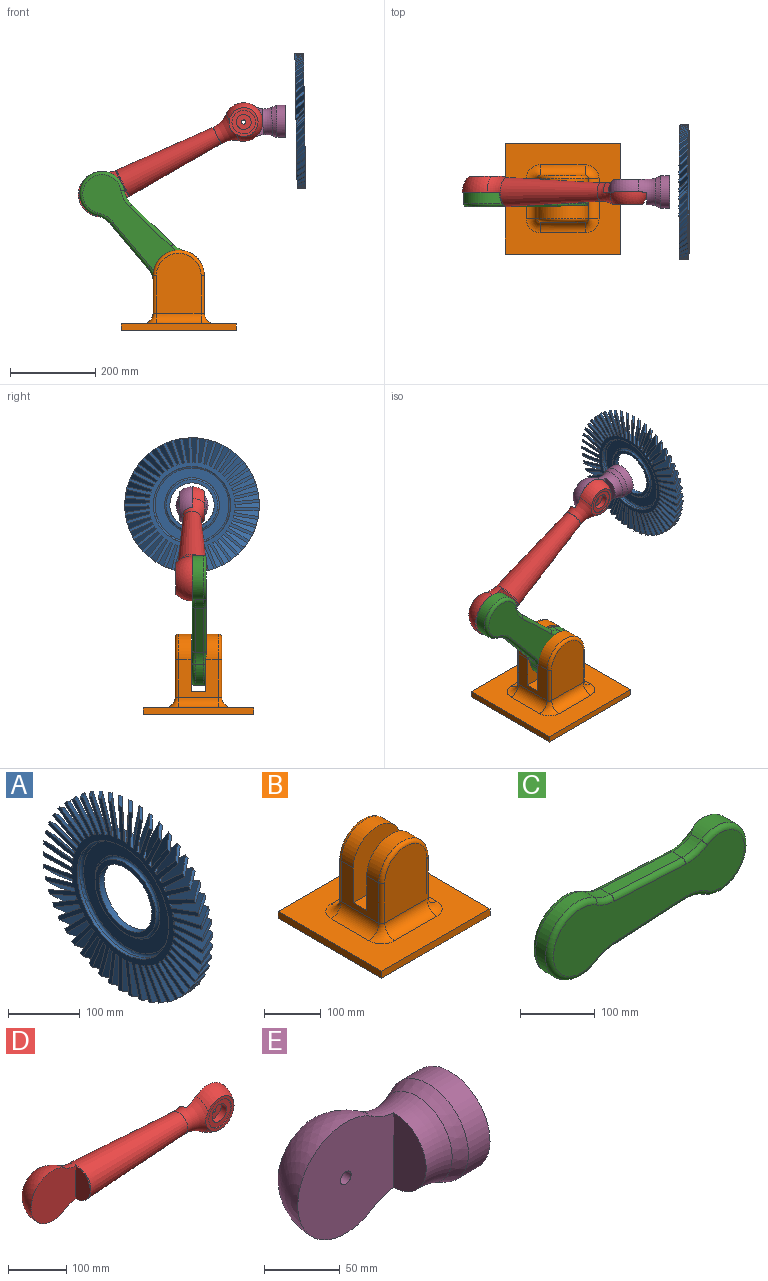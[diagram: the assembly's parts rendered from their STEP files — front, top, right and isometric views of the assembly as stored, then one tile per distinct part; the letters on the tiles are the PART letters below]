
ASSEMBLY  parts=5 mates=4
PART A: 209 faces, bbox 20x315.1x315 mm
  f0: cylinder r=90.5mm len=181mm, axis (-1,0,0), area 2843.1mm2, adj f1,f2
  f1: plane 314.99x314.87mm, normal (1,0,0), area 25655mm2, adj f0,f3,f4,f5,f6,f7,f8,f9
  f2: torus R=86.5mm, axis (-1,0,0), area 3515.4mm2, adj f0,f199
  f3: cylinder r=157.5mm len=25.8mm, axis (-1,0,0), area 130.3mm2, adj f1,f4,f198,f200
  f4: plane 60.82x29.89mm, normal (-0.71,0.7,-0.13), area 1610.9mm2, adj f1,f3,f5,f200
  f5: plane 24.82x20mm, normal (0,0.25,0.97), area 113.1mm2, adj f1,f4,f6,f200
  f6: plane 59.18x37.22mm, normal (0.71,-0.67,0.23), area 1598.6mm2, adj f1,f5,f7,f200
  f7: cylinder r=157.5mm len=24.84mm, axis (-1,0,0), area 130.3mm2, adj f1,f6,f8,f200
  f8: plane 61.46x36.15mm, normal (-0.71,0.67,-0.22), area 1610.9mm2, adj f1,f7,f9,f200
  f9: plane 23.78x20mm, normal (0,0.38,0.93), area 113.1mm2, adj f1,f8,f10,f200
  f10: plane 58.82x43mm, normal (0.71,-0.64,0.31), area 1598.6mm2, adj f1,f9,f11,f200
  f11: cylinder r=157.5mm len=23.47mm, axis (-1,0,0), area 130.3mm2, adj f1,f10,f12,f200
  f12: plane 61.08x41.82mm, normal (-0.71,0.64,-0.3), area 1610.9mm2, adj f1,f11,f13,f200
  f13: plane 22.36x20mm, normal (0,0.49,0.87), area 113.1mm2, adj f1,f12,f14,f200
  f14: plane 57.5x48.08mm, normal (0.71,-0.59,0.39), area 1598.6mm2, adj f1,f13,f15,f200
  f15: cylinder r=157.5mm len=21.71mm, axis (-1,0,0), area 130.3mm2, adj f1,f14,f16,f200
  f16: plane 59.71x46.8mm, normal (-0.71,0.6,-0.38), area 1610.9mm2, adj f1,f15,f17,f200
  f17: plane 20.56x20mm, normal (0,0.6,0.8), area 113.1mm2, adj f1,f16,f18,f200
  f18: plane 55.23x52.37mm, normal (0.71,-0.54,0.46), area 1598.6mm2, adj f1,f17,f19,f200
  f19: cylinder r=157.5mm len=20mm, axis (-1,0,0), area 130.3mm2, adj f1,f18,f20,f200
  f20: plane 57.35x51.02mm, normal (-0.71,0.54,-0.46), area 1610.9mm2, adj f1,f19,f21,f200
  f21: plane 20x18.43mm, normal (0,0.7,0.72), area 113.1mm2, adj f1,f20,f22,f200
  f22: plane 55.79x52.05mm, normal (0.71,-0.47,0.53), area 1598.6mm2, adj f1,f21,f23,f200
  f23: cylinder r=157.5mm len=20.15mm, axis (-1,0,0), area 130.3mm2, adj f1,f22,f24,f200
  f24: plane 54.39x54.05mm, normal (-0.71,0.48,-0.52), area 1610.9mm2, adj f1,f23,f25,f200
  f25: plane 20.06x20mm, normal (0,0.78,0.62), area 113.1mm2, adj f1,f24,f26,f200
  f26: plane 58.31x48.02mm, normal (0.71,-0.4,0.58), area 1598.6mm2, adj f1,f25,f27,f200
  f27: cylinder r=157.5mm len=22.18mm, axis (-1,0,0), area 130.3mm2, adj f1,f26,f28,f200
  f28: plane 56.88x49.87mm, normal (-0.71,0.41,-0.58), area 1610.9mm2, adj f1,f27,f29,f200
  f29: plane 21.94x20mm, normal (0,0.86,0.52), area 113.1mm2, adj f1,f28,f30,f200
  f30: plane 59.86x43.2mm, normal (0.71,-0.32,0.63), area 1598.6mm2, adj f1,f29,f31,f200
  f31: cylinder r=157.5mm len=23.84mm, axis (-1,0,0), area 130.3mm2, adj f1,f30,f32,f200
  f32: plane 58.43x44.86mm, normal (-0.71,0.33,-0.63), area 1610.9mm2, adj f1,f31,f33,f200
  f33: plane 23.46x20mm, normal (0,0.91,0.4), area 113.1mm2, adj f1,f32,f34,f200
  f34: plane 60.43x37.68mm, normal (0.71,-0.24,0.67), area 1598.6mm2, adj f1,f33,f35,f200
  f35: cylinder r=157.5mm len=25.12mm, axis (-1,0,0), area 130.3mm2, adj f1,f34,f36,f200
  f36: plane 59.02x39.13mm, normal (-0.71,0.25,-0.66), area 1610.9mm2, adj f1,f35,f37,f200
  f37: plane 24.6x20mm, normal (0,0.96,0.28), area 113.1mm2, adj f1,f36,f38,f200
  f38: plane 60.01x31.53mm, normal (0.71,-0.15,0.69), area 1598.6mm2, adj f1,f37,f39,f200
  f39: cylinder r=157.5mm len=25.98mm, axis (-1,0,0), area 130.3mm2, adj f1,f38,f40,f200
  f40: plane 58.64x32.74mm, normal (-0.71,0.16,-0.69), area 1610.9mm2, adj f1,f39,f41,f200
  f41: plane 25.33x20mm, normal (0,0.99,0.16), area 113.1mm2, adj f1,f40,f42,f200
  f42: plane 58.6x24.87mm, normal (0.71,-0.06,0.71), area 1598.6mm2, adj f1,f41,f43,f200
  f43: cylinder r=157.5mm len=26.41mm, axis (-1,0,0), area 130.3mm2, adj f1,f42,f44,f200
  f44: plane 57.35x25.83mm, normal (-0.71,0.07,-0.7), area 1610.9mm2, adj f1,f43,f45,f200
  f45: plane 25.64x20mm, normal (0,1,0.03), area 113.1mm2, adj f1,f44,f46,f200
  f46: plane 57.14x22.14mm, normal (0.71,0.03,0.71), area 1598.6mm2, adj f1,f45,f47,f200
  f47: cylinder r=157.5mm len=26.41mm, axis (-1,0,0), area 130.3mm2, adj f1,f46,f48,f200
  f48: plane 58.63x21.39mm, normal (-0.71,-0.02,-0.71), area 1610.9mm2, adj f1,f47,f49,f200
  f49: plane 25.54x20mm, normal (0,1,-0.1), area 113.1mm2, adj f1,f48,f50,f200
  f50: plane 58.26x29.15mm, normal (0.71,0.12,0.7), area 1598.6mm2, adj f1,f49,f51,f200
  f51: cylinder r=157.5mm len=25.98mm, axis (-1,0,0), area 130.3mm2, adj f1,f50,f52,f200
  f52: plane 60.5x28.25mm, normal (-0.71,-0.11,-0.7), area 1610.9mm2, adj f1,f51,f53,f200
  f53: plane 25.01x20mm, normal (0,0.97,-0.22), area 113.1mm2, adj f1,f52,f54,f200
  f54: plane 59.12x35.68mm, normal (0.71,0.21,0.68), area 1598.6mm2, adj f1,f53,f55,f200
  f55: cylinder r=157.5mm len=25.12mm, axis (-1,0,0), area 130.3mm2, adj f1,f54,f56,f200
  f56: plane 61.39x34.64mm, normal (-0.71,-0.2,-0.68), area 1610.9mm2, adj f1,f55,f57,f200
  f57: plane 24.08x20mm, normal (0,0.94,-0.35), area 113.1mm2, adj f1,f56,f58,f200
  f58: plane 59x41.62mm, normal (0.71,0.29,0.65), area 1598.6mm2, adj f1,f57,f59,f200
  f59: cylinder r=157.5mm len=23.85mm, axis (-1,0,0), area 130.3mm2, adj f1,f58,f60,f200
  f60: plane 61.27x40.47mm, normal (-0.71,-0.28,-0.65), area 1610.9mm2, adj f1,f59,f61,f200
  f61: plane 22.75x20mm, normal (0,0.89,-0.46), area 113.1mm2, adj f1,f60,f62,f200
  f62: plane 57.92x46.88mm, normal (0.71,0.37,0.6), area 1598.6mm2, adj f1,f61,f63,f200
  f63: cylinder r=157.5mm len=22.18mm, axis (-1,0,0), area 130.3mm2, adj f1,f62,f64,f200
  f64: plane 60.14x45.63mm, normal (-0.71,-0.36,-0.61), area 1610.9mm2, adj f1,f63,f65,f200
  f65: plane 21.04x20mm, normal (0,0.82,-0.57), area 113.1mm2, adj f1,f64,f66,f200
  f66: plane 55.88x51.37mm, normal (0.71,0.45,0.55), area 1598.6mm2, adj f1,f65,f67,f200
  f67: cylinder r=157.5mm len=20.16mm, axis (-1,0,0), area 130.3mm2, adj f1,f66,f68,f200
  f68: plane 58.03x50.04mm, normal (-0.71,-0.44,-0.56), area 1610.9mm2, adj f1,f67,f69,f200
  f69: plane 20x18.99mm, normal (0,0.74,-0.67), area 113.1mm2, adj f1,f68,f70,f200
  f70: plane 55.02x52.93mm, normal (0.71,0.51,0.49), area 1598.6mm2, adj f1,f69,f71,f200
  f71: cylinder r=157.5mm len=20mm, axis (-1,0,0), area 130.3mm2, adj f1,f70,f72,f200
  f72: plane 54.96x53.63mm, normal (-0.71,-0.51,-0.5), area 1610.9mm2, adj f1,f71,f73,f200
  f73: plane 20x19.54mm, normal (0,0.65,-0.76), area 113.1mm2, adj f1,f72,f74,f200
  f74: plane 57.77x49.11mm, normal (0.71,0.57,0.42), area 1598.6mm2, adj f1,f73,f75,f200
  f75: cylinder r=157.5mm len=21.7mm, axis (-1,0,0), area 130.3mm2, adj f1,f74,f76,f200
  f76: plane 56.34x50.99mm, normal (-0.71,-0.56,-0.43), area 1610.9mm2, adj f1,f75,f77,f200
  f77: plane 21.5x20mm, normal (0,0.55,-0.84), area 113.1mm2, adj f1,f76,f78,f200
  f78: plane 59.56x44.48mm, normal (0.71,0.62,0.34), area 1598.6mm2, adj f1,f77,f79,f200
  f79: cylinder r=157.5mm len=23.46mm, axis (-1,0,0), area 130.3mm2, adj f1,f78,f80,f200
  f80: plane 58.13x46.19mm, normal (-0.71,-0.61,-0.35), area 1610.9mm2, adj f1,f79,f81,f200
  f81: plane 23.12x20mm, normal (0,0.43,-0.9), area 113.1mm2, adj f1,f80,f82,f200
  f82: plane 60.38x39.12mm, normal (0.71,0.66,0.26), area 1598.6mm2, adj f1,f81,f83,f200
  f83: cylinder r=157.5mm len=24.84mm, axis (-1,0,0), area 130.3mm2, adj f1,f82,f84,f200
  f84: plane 58.96x40.62mm, normal (-0.71,-0.65,-0.27), area 1610.9mm2, adj f1,f83,f85,f200
  f85: plane 24.35x20mm, normal (0,0.32,-0.95), area 113.1mm2, adj f1,f84,f86,f200
  f86: plane 60.21x33.12mm, normal (0.71,0.69,0.18), area 1598.6mm2, adj f1,f85,f87,f200
  f87: cylinder r=157.5mm len=25.8mm, axis (-1,0,0), area 130.3mm2, adj f1,f86,f88,f200
  f88: plane 58.82x34.39mm, normal (-0.71,-0.68,-0.18), area 1610.9mm2, adj f1,f87,f89,f200
  f89: plane 25.18x20mm, normal (0,0.19,-0.98), area 113.1mm2, adj f1,f88,f90,f200
  f90: plane 59.05x26.57mm, normal (0.71,0.7,0.09), area 1598.6mm2, adj f1,f89,f91,f200
  f91: cylinder r=157.5mm len=26.34mm, axis (-1,0,0), area 130.3mm2, adj f1,f90,f92,f200
  f92: plane 57.72x27.6mm, normal (-0.71,-0.7,-0.1), area 1610.9mm2, adj f1,f91,f93,f200
  f93: plane 25.6x20mm, normal (0,0.06,-1), area 113.1mm2, adj f1,f92,f94,f200
  f94: plane 57.37x20.32mm, normal (0.71,0.71,0), area 1598.6mm2, adj f1,f93,f95,f200
  f95: cylinder r=157.5mm len=26.45mm, axis (-1,0,0), area 130.3mm2, adj f1,f94,f96,f200
  f96: plane 58.03x20.35mm, normal (-0.71,-0.71,0), area 1610.9mm2, adj f1,f95,f97,f200
  f97: plane 25.6x20mm, normal (0,-0.06,-1), area 113.1mm2, adj f1,f96,f98,f200
  f98: plane 57.9x27.43mm, normal (0.71,0.7,-0.1), area 1598.6mm2, adj f1,f97,f99,f200
  f99: cylinder r=157.5mm len=26.13mm, axis (-1,0,0), area 130.3mm2, adj f1,f98,f100,f200
  f100: plane 60.13x26.57mm, normal (-0.71,-0.7,0.09), area 1610.9mm2, adj f1,f99,f101,f200
  f101: plane 25.18x20mm, normal (0,-0.19,-0.98), area 113.1mm2, adj f1,f100,f102,f200
  f102: plane 59x34.1mm, normal (0.71,0.68,-0.18), area 1598.6mm2, adj f1,f101,f103,f200
  f103: cylinder r=157.5mm len=25.37mm, axis (-1,0,0), area 130.3mm2, adj f1,f102,f104,f200
  f104: plane 61.26x33.09mm, normal (-0.71,-0.69,0.18), area 1610.9mm2, adj f1,f103,f105,f200
  f105: plane 24.35x20mm, normal (0,-0.32,-0.95), area 113.1mm2, adj f1,f104,f106,f200
  f106: plane 59.12x40.2mm, normal (0.71,0.65,-0.27), area 1598.6mm2, adj f1,f105,f107,f200
  f107: cylinder r=157.5mm len=24.2mm, axis (-1,0,0), area 130.3mm2, adj f1,f106,f108,f200
  f108: plane 61.39x39.07mm, normal (-0.71,-0.66,0.26), area 1610.9mm2, adj f1,f107,f109,f200
  f109: plane 23.12x20mm, normal (0,-0.43,-0.9), area 113.1mm2, adj f1,f108,f110,f200
  f110: plane 58.28x45.64mm, normal (0.71,0.61,-0.35), area 1598.6mm2, adj f1,f109,f111,f200
  f111: cylinder r=157.5mm len=22.64mm, axis (-1,0,0), area 130.3mm2, adj f1,f110,f112,f200
  f112: plane 60.52x44.4mm, normal (-0.71,-0.62,0.34), area 1610.9mm2, adj f1,f111,f113,f200
  f113: plane 21.5x20mm, normal (0,-0.55,-0.84), area 113.1mm2, adj f1,f112,f114,f200
  f114: plane 56.48x50.33mm, normal (0.71,0.56,-0.43), area 1598.6mm2, adj f1,f113,f115,f200
  f115: cylinder r=157.5mm len=20.7mm, axis (-1,0,0), area 130.3mm2, adj f1,f114,f116,f200
  f116: plane 58.65x49.01mm, normal (-0.71,-0.57,0.42), area 1610.9mm2, adj f1,f115,f117,f200
  f117: plane 20x19.54mm, normal (0,-0.65,-0.76), area 113.1mm2, adj f1,f116,f118,f200
  f118: plane 54.19x53.75mm, normal (0.71,0.51,-0.5), area 1598.6mm2, adj f1,f117,f119,f200
  f119: cylinder r=157.5mm len=20mm, axis (-1,0,0), area 130.3mm2, adj f1,f118,f120,f200
  f120: plane 55.82x52.81mm, normal (-0.71,-0.51,0.49), area 1610.9mm2, adj f1,f119,f121,f200
  f121: plane 20x18.99mm, normal (0,-0.74,-0.67), area 113.1mm2, adj f1,f120,f122,f200
  f122: plane 57.17x50.14mm, normal (0.71,0.44,-0.56), area 1598.6mm2, adj f1,f121,f123,f200
  f123: cylinder r=157.5mm len=21.21mm, axis (-1,0,0), area 130.3mm2, adj f1,f122,f124,f200
  f124: plane 55.75x52.07mm, normal (-0.71,-0.45,0.55), area 1610.9mm2, adj f1,f123,f125,f200
  f125: plane 21.04x20mm, normal (0,-0.82,-0.57), area 113.1mm2, adj f1,f124,f126,f200
  f126: plane 59.2x45.71mm, normal (0.71,0.36,-0.61), area 1598.6mm2, adj f1,f125,f127,f200
  f127: cylinder r=157.5mm len=23.06mm, axis (-1,0,0), area 130.3mm2, adj f1,f126,f128,f200
  f128: plane 57.77x47.46mm, normal (-0.71,-0.37,0.6), area 1610.9mm2, adj f1,f127,f129,f200
  f129: plane 22.75x20mm, normal (0,-0.89,-0.46), area 113.1mm2, adj f1,f128,f130,f200
  f130: plane 60.27x40.52mm, normal (0.71,0.28,-0.65), area 1598.6mm2, adj f1,f129,f131,f200
  f131: cylinder r=157.5mm len=24.53mm, axis (-1,0,0), area 130.3mm2, adj f1,f130,f132,f200
  f132: plane 58.84x42.08mm, normal (-0.71,-0.29,0.65), area 1610.9mm2, adj f1,f131,f133,f200
  f133: plane 24.08x20mm, normal (0,-0.94,-0.35), area 113.1mm2, adj f1,f132,f134,f200
  f134: plane 60.34x34.67mm, normal (0.71,0.2,-0.68), area 1598.6mm2, adj f1,f133,f135,f200
  f135: cylinder r=157.5mm len=25.6mm, axis (-1,0,0), area 130.3mm2, adj f1,f134,f136,f200
  f136: plane 58.95x36.01mm, normal (-0.71,-0.21,0.68), area 1610.9mm2, adj f1,f135,f137,f200
  f137: plane 25.01x20mm, normal (0,-0.97,-0.22), area 113.1mm2, adj f1,f136,f138,f200
  f138: plane 59.43x28.26mm, normal (0.71,0.11,-0.7), area 1598.6mm2, adj f1,f137,f139,f200
  f139: cylinder r=157.5mm len=26.25mm, axis (-1,0,0), area 130.3mm2, adj f1,f138,f140,f200
  f140: plane 58.09x29.35mm, normal (-0.71,-0.12,0.7), area 1610.9mm2, adj f1,f139,f141,f200
  f141: plane 25.54x20mm, normal (0,-1,-0.1), area 113.1mm2, adj f1,f140,f142,f200
  f142: plane 57.7x21.37mm, normal (0.71,0.02,-0.71), area 1598.6mm2, adj f1,f141,f143,f200
  f143: cylinder r=157.5mm len=26.47mm, axis (-1,0,0), area 130.3mm2, adj f1,f142,f144,f200
  f144: plane 57.49x22.2mm, normal (-0.71,-0.03,0.71), area 1610.9mm2, adj f1,f143,f145,f200
  f145: plane 25.64x20mm, normal (0,-1,0.03), area 113.1mm2, adj f1,f144,f146,f200
  f146: plane 57.48x25.7mm, normal (0.71,-0.07,-0.7), area 1598.6mm2, adj f1,f145,f147,f200
  f147: cylinder r=157.5mm len=26.25mm, axis (-1,0,0), area 130.3mm2, adj f1,f146,f148,f200
  f148: plane 59.69x24.87mm, normal (-0.71,0.06,0.71), area 1610.9mm2, adj f1,f147,f149,f200
  f149: plane 25.33x20mm, normal (0,-0.99,0.16), area 113.1mm2, adj f1,f148,f150,f200
  f150: plane 58.81x32.48mm, normal (0.71,-0.16,-0.69), area 1598.6mm2, adj f1,f149,f151,f200
  f151: cylinder r=157.5mm len=25.6mm, axis (-1,0,0), area 130.3mm2, adj f1,f150,f152,f200
  f152: plane 61.07x31.51mm, normal (-0.71,0.15,0.69), area 1610.9mm2, adj f1,f151,f153,f200
  f153: plane 24.6x20mm, normal (0,-0.96,0.28), area 113.1mm2, adj f1,f152,f154,f200
  f154: plane 59.18x38.73mm, normal (0.71,-0.25,-0.66), area 1598.6mm2, adj f1,f153,f155,f200
  f155: cylinder r=157.5mm len=24.53mm, axis (-1,0,0), area 130.3mm2, adj f1,f154,f156,f200
  f156: plane 61.46x37.63mm, normal (-0.71,0.24,0.67), area 1610.9mm2, adj f1,f155,f157,f200
  f157: plane 23.46x20mm, normal (0,-0.91,0.4), area 113.1mm2, adj f1,f156,f158,f200
  f158: plane 58.58x44.34mm, normal (0.71,-0.33,-0.63), area 1598.6mm2, adj f1,f157,f159,f200
  f159: cylinder r=157.5mm len=23.06mm, axis (-1,0,0), area 130.3mm2, adj f1,f158,f160,f200
  f160: plane 60.83x43.14mm, normal (-0.71,0.32,0.63), area 1610.9mm2, adj f1,f159,f161,f200
  f161: plane 21.94x20mm, normal (0,-0.86,0.52), area 113.1mm2, adj f1,f160,f162,f200
  f162: plane 57.02x49.23mm, normal (0.71,-0.41,-0.58), area 1598.6mm2, adj f1,f161,f163,f200
  f163: cylinder r=157.5mm len=21.21mm, axis (-1,0,0), area 130.3mm2, adj f1,f162,f164,f200
  f164: plane 59.21x47.93mm, normal (-0.71,0.4,0.58), area 1610.9mm2, adj f1,f163,f165,f200
  f165: plane 20.06x20mm, normal (0,-0.78,0.62), area 113.1mm2, adj f1,f164,f166,f200
  f166: plane 54.52x53.31mm, normal (0.71,-0.48,-0.52), area 1598.6mm2, adj f1,f165,f167,f200
  f167: cylinder r=157.5mm len=20mm, axis (-1,0,0), area 130.3mm2, adj f1,f166,f168,f200
  f168: plane 56.61x51.94mm, normal (-0.71,0.47,0.53), area 1610.9mm2, adj f1,f167,f169,f200
  f169: plane 20x18.43mm, normal (0,-0.7,0.72), area 113.1mm2, adj f1,f168,f170,f200
  f170: plane 56.51x51.12mm, normal (0.71,-0.54,-0.46), area 1598.6mm2, adj f1,f169,f171,f200
  f171: cylinder r=157.5mm len=20.69mm, axis (-1,0,0), area 130.3mm2, adj f1,f170,f172,f200
  f172: plane 55.1x53.09mm, normal (-0.71,0.54,0.46), area 1610.9mm2, adj f1,f171,f173,f200
  f173: plane 20.56x20mm, normal (0,-0.6,0.8), area 113.1mm2, adj f1,f172,f174,f200
  f174: plane 58.79x46.89mm, normal (0.71,-0.6,-0.38), area 1598.6mm2, adj f1,f173,f175,f200
  f175: cylinder r=157.5mm len=22.63mm, axis (-1,0,0), area 130.3mm2, adj f1,f174,f176,f200
  f176: plane 57.35x48.69mm, normal (-0.71,0.59,0.39), area 1610.9mm2, adj f1,f175,f177,f200
  f177: plane 22.36x20mm, normal (0,-0.49,0.87), area 113.1mm2, adj f1,f176,f178,f200
  f178: plane 60.09x41.89mm, normal (0.71,-0.64,-0.3), area 1598.6mm2, adj f1,f177,f179,f200
  f179: cylinder r=157.5mm len=24.2mm, axis (-1,0,0), area 130.3mm2, adj f1,f178,f180,f200
  f180: plane 58.66x43.5mm, normal (-0.71,0.64,0.31), area 1610.9mm2, adj f1,f179,f181,f200
  f181: plane 23.78x20mm, normal (0,-0.38,0.93), area 113.1mm2, adj f1,f180,f182,f200
  f182: plane 60.42x36.19mm, normal (0.71,-0.67,-0.22), area 1598.6mm2, adj f1,f181,f183,f200
  f183: cylinder r=157.5mm len=25.37mm, axis (-1,0,0), area 130.3mm2, adj f1,f182,f184,f200
  f184: plane 59.01x37.59mm, normal (-0.71,0.67,0.23), area 1610.9mm2, adj f1,f183,f185,f200
  f185: plane 24.82x20mm, normal (0,-0.25,0.97), area 113.1mm2, adj f1,f184,f186,f200
  f186: plane 59.75x29.91mm, normal (0.71,-0.7,-0.13), area 1598.6mm2, adj f1,f185,f187,f200
  f187: cylinder r=157.5mm len=26.13mm, axis (-1,0,0), area 130.3mm2, adj f1,f186,f188,f200
  f188: plane 58.39x31.06mm, normal (-0.71,0.69,0.14), area 1610.9mm2, adj f1,f187,f189,f200
  f189: plane 25.45x20mm, normal (0,-0.13,0.99), area 113.1mm2, adj f1,f188,f190,f200
  f190: plane 58.11x23.13mm, normal (0.71,-0.71,-0.04), area 1598.6mm2, adj f1,f189,f191,f200
  f191: cylinder r=157.5mm len=26.45mm, axis (-1,0,0), area 130.2mm2, adj f1,f190,f192,f200
  f192: plane 57.01x24.01mm, normal (-0.71,0.71,0.05), area 1610.9mm2, adj f1,f191,f193,f200
  f193: plane 25.66x20mm, normal (0,0,1), area 113.1mm2, adj f1,f192,f194,f200
  f194: plane 56.99x23.93mm, normal (0.71,-0.71,0.05), area 1598.6mm2, adj f1,f193,f195,f200
  f195: cylinder r=157.5mm len=26.34mm, axis (-1,0,0), area 130.3mm2, adj f1,f194,f196,f200
  f196: plane 59.19x23.14mm, normal (-0.71,0.71,-0.04), area 1610.9mm2, adj f1,f195,f197,f200
  f197: plane 25.45x20mm, normal (0,0.13,0.99), area 113.1mm2, adj f1,f196,f198,f200
  f198: plane 58.57x30.83mm, normal (0.71,-0.69,0.14), area 1598.6mm2, adj f1,f3,f197,f200
  f199: plane 175.32x173.01mm, normal (1,0,0), area 10638.2mm2, adj f2,f201
  f200: plane 314.98x314.86mm, normal (-1,0,0), area 25230.5mm2, adj f3,f4,f5,f6,f7,f8,f9,f10
  f201: torus R=64mm, axis (-1,0,0), area 2426.1mm2, adj f199,f203
  f202: cylinder r=90.5mm len=181mm, axis (-1,0,0), area 2843.1mm2, adj f200,f204
  f203: plane 122.22x120mm, normal (1,0,0), area 2814.9mm2, adj f201,f205
  f204: torus R=86.5mm, axis (-1,0,0), area 3515.5mm2, adj f202,f206
  f205: cylinder r=52mm len=104mm, axis (-1,0,0), area 3267.3mm2, adj f203,f207
  f206: plane 176.2x173mm, normal (-1,0,0), area 10638.2mm2, adj f204,f208
  f207: plane 122.22x120mm, normal (-1,0,0), area 2814.9mm2, adj f205,f208
  f208: torus R=64mm, axis (-1,0,0), area 2426.1mm2, adj f206,f207
PART B: 29 faces, bbox 270x258.8x192.4 mm
  f0: plane 270x258.75mm, normal (0,0,-1), area 69862.5mm2, adj f8,f9,f10,f11
  f1: torus R=52.5mm, axis (0,-1,0), area 2119.8mm2, adj f6,f13,f14,f15
  f2: cylinder r=60mm len=120mm, axis (0,1,0), area 5654.9mm2, adj f3,f7,f12,f16
  f3: plane 135x120mm, normal (0,-1,0), area 14654.7mm2, adj f2,f4,f12,f16
  f4: plane 120x33.75mm, normal (0,0,1), area 4050mm2, adj f3,f5,f12,f16
  f5: plane 135x120mm, normal (0,1,0), area 14654.8mm2, adj f4,f6,f12,f16
  f6: cylinder r=60mm len=120mm, axis (0,1,0), area 5654.9mm2, adj f1,f5,f12,f16
  f7: torus R=52.5mm, axis (0,-1,0), area 2119.8mm2, adj f2,f17,f18,f19
  f8: plane 270x15mm, normal (0,-1,0), area 4050mm2, adj f0,f9,f11,f20
  f9: plane 258.75x15mm, normal (1,0,0), area 3881.2mm2, adj f0,f8,f10,f20
  f10: plane 270x15mm, normal (0,1,0), area 4050mm2, adj f0,f9,f11,f20
  f11: plane 258.75x15mm, normal (-1,0,0), area 3881.2mm2, adj f0,f8,f10,f20
  f12: plane 93.75x87.5mm, normal (1,0,0), area 5671.9mm2, adj f2,f3,f4,f5,f6,f13,f19,f24
  f13: cylinder r=7.5mm len=87.5mm, axis (0,0,-1), area 1030.8mm2, adj f1,f12,f14,f26
  f14: plane 140x105mm, normal (0,-1,0), area 13517mm2, adj f1,f13,f15,f28
  f15: cylinder r=7.5mm len=87.5mm, axis (0,0,-1), area 1030.8mm2, adj f1,f14,f16,f27
  f16: plane 93.75x87.5mm, normal (-1,0,0), area 5671.9mm2, adj f2,f3,f4,f5,f6,f15,f17,f25
  f17: cylinder r=7.5mm len=87.5mm, axis (0,0,-1), area 1030.8mm2, adj f7,f16,f18,f23
  f18: plane 140x105mm, normal (0,1,0), area 13517mm2, adj f7,f17,f19,f21
  f19: cylinder r=7.5mm len=87.5mm, axis (0,0,-1), area 1030.8mm2, adj f7,f12,f18,f22
  f20: plane 270x258.75mm, normal (0,0,1), area 43781.7mm2, adj f8,f9,f10,f11,f21,f22,f23,f24
  f21: cylinder r=25mm len=105mm, axis (1,0,0), area 4123.3mm2, adj f18,f20,f22,f23
  f22: torus R=32.5mm, axis (0,0,1), area 1023mm2, adj f19,f20,f21,f24
  f23: torus R=32.5mm, axis (0,0,1), area 1023mm2, adj f17,f20,f21,f25
  f24: cylinder r=25mm len=93.75mm, axis (0,1,0), area 3681.6mm2, adj f12,f20,f22,f26
  f25: cylinder r=25mm len=93.75mm, axis (0,1,0), area 3681.6mm2, adj f16,f20,f23,f27
  f26: torus R=32.5mm, axis (0,0,1), area 1023mm2, adj f13,f20,f24,f28
  f27: torus R=32.5mm, axis (0,0,1), area 1023mm2, adj f15,f20,f25,f28
  f28: cylinder r=25mm len=105mm, axis (1,0,0), area 4123.3mm2, adj f14,f20,f26,f27
PART C: 25 faces, bbox 384.2x33.8x129.8 mm
  f0: cylinder r=60mm len=29.46mm, axis (0,1,0), area 587.3mm2, adj f1,f3,f6,f9
  f1: plane 134.99x18.75mm, normal (0.05,0,-1), area 2534.5mm2, adj f0,f2,f8,f12
  f2: cylinder r=7.5mm len=135.38mm, axis (-1,0,-0.05), area 1592.5mm2, adj f1,f3,f5,f14
  f3: torus R=67.5mm, axis (0,1,0), area 385.8mm2, adj f0,f2,f4,f14
  f4: torus R=52.5mm, axis (0,1,0), area 2894.9mm2, adj f3,f6,f7,f14
  f5: torus R=67.5mm, axis (0,1,0), area 472.5mm2, adj f2,f12,f14,f15
  f6: cylinder r=60mm len=120mm, axis (0,1,0), area 4826.7mm2, adj f0,f4,f10,f16
  f7: torus R=67.5mm, axis (0,1,0), area 385.8mm2, adj f4,f14,f16,f17
  f8: cylinder r=7.5mm len=135.38mm, axis (-1,0,-0.05), area 1592.5mm2, adj f1,f9,f13,f18
  f9: torus R=67.5mm, axis (0,1,0), area 385.8mm2, adj f0,f8,f10,f18
  f10: torus R=52.5mm, axis (0,1,0), area 2894.9mm2, adj f6,f9,f11,f18
  f11: torus R=67.5mm, axis (0,1,0), area 385.8mm2, adj f10,f16,f18,f19
  f12: cylinder r=60mm len=36.37mm, axis (0,1,0), area 719.3mm2, adj f1,f5,f13,f20
  f13: torus R=67.5mm, axis (0,1,0), area 590mm2, adj f8,f12,f18,f20
  f14: plane 361.5x106.61mm, normal (0,-1,0), area 25390.2mm2, adj f2,f3,f4,f5,f7,f15,f17,f21
  f15: torus R=45mm, axis (0,1,0), area 2530.6mm2, adj f5,f14,f20,f21
  f16: cylinder r=60mm len=29.46mm, axis (0,1,0), area 587.3mm2, adj f6,f7,f11,f22
  f17: cylinder r=7.5mm len=135.38mm, axis (-1,0,0.05), area 1592.5mm2, adj f7,f14,f21,f22
  f18: plane 368.84x106.61mm, normal (0,1,0), area 26759.7mm2, adj f8,f9,f10,f11,f13,f19,f20,f23
  f19: cylinder r=7.5mm len=135.38mm, axis (-1,0,0.05), area 1592.5mm2, adj f11,f18,f22,f23
  f20: cylinder r=52.5mm len=105mm, axis (0,1,0), area 5787.9mm2, adj f12,f13,f15,f18,f23,f24
  f21: torus R=67.5mm, axis (0,1,0), area 472.5mm2, adj f14,f15,f17,f24
  f22: plane 134.99x18.75mm, normal (0.05,0,1), area 2534.5mm2, adj f16,f17,f19,f24
  f23: torus R=67.5mm, axis (0,1,0), area 590mm2, adj f18,f19,f20,f24
  f24: cylinder r=60mm len=36.37mm, axis (0,1,0), area 719.3mm2, adj f20,f21,f22,f23
PART D: 16 faces, bbox 472.5x111.7x111.7 mm
  f0: cylinder r=17.5mm len=35mm, axis (0,-1,0), area 1429.4mm2, adj f1,f2
  f1: plane 35.65x35mm, normal (0,-1,0), area 883.6mm2, adj f0,f3
  f2: plane 56.02x55mm, normal (0,-1,0), area 1413.7mm2, adj f0,f4
  f3: cylinder r=5mm len=15mm, axis (0,-1,0), area 471.2mm2, adj f1,f6
  f4: cylinder r=27.5mm len=55mm, axis (0,-1,0), area 345.6mm2, adj f2,f9
  f5: plane 78.64x73.55mm, normal (0,1,0), area 4358.8mm2, adj f10,f14
  f6: plane 97.5x90.1mm, normal (0,1,0), area 6814.7mm2, adj f3,f7,f8,f13
  f7: plane 45.8x23.02mm, normal (1,0,0), area 823.6mm2, adj f6,f13
  f8: sphere r=45mm, area 6320.7mm2, adj f6,f9,f13
  f9: plane 68.91x67.15mm, normal (0,-1,0), area 1190.8mm2, adj f4,f8,f13
  f10: sphere r=52.5mm, area 8775.7mm2, adj f5,f11,f14
  f11: plane 108.75x105.12mm, normal (0,-1,0), area 9274.4mm2, adj f10,f12,f14
  f12: plane 68.82x34.53mm, normal (-1,0,0), area 1860mm2, adj f11,f14
  f13: torus R=81.24mm, axis (1,0,0), area 4535.4mm2, adj f6,f7,f8,f9,f15
  f14: torus R=94.18mm, axis (1,0,0), area 3552.4mm2, adj f5,f10,f11,f12,f15
  f15: cone r=21.32mm half-angle=3deg, axis (-1,0,0), area 43174.9mm2, adj f13,f14
PART E: 13 faces, bbox 142.5x93.2x93.2 mm
  f0: cylinder r=17.5mm len=35mm, axis (0,1,0), area 1429.4mm2, adj f1,f3
  f1: plane 35.65x35mm, normal (0,1,0), area 883.6mm2, adj f0,f4
  f2: plane 75.98x75.98mm, normal (1,0,0), area 4417.9mm2, adj f5
  f3: plane 56.02x55mm, normal (0,1,0), area 1413.7mm2, adj f0,f6
  f4: cylinder r=5mm len=15mm, axis (0,1,0), area 471.2mm2, adj f1,f7
  f5: cylinder r=37.5mm len=75mm, axis (-1,0,0), area 4770.9mm2, adj f2,f9
  f6: cylinder r=27.5mm len=55mm, axis (0,1,0), area 345.6mm2, adj f3,f11
  f7: plane 90.09x90mm, normal (0,-1,0), area 6547.8mm2, adj f4,f8,f10,f12
  f8: plane 60.5x30.33mm, normal (-1,0,0), area 1437.5mm2, adj f7,f12
  f9: cone r=33.17mm half-angle=21.6deg, axis (1,0,0), area 2604.7mm2, adj f5,f12
  f10: sphere r=45mm, area 6000.6mm2, adj f7,f11,f12
  f11: plane 83.08x67.15mm, normal (0,1,0), area 1422.2mm2, adj f6,f10,f12
  f12: torus R=75mm, axis (-1,0,0), area 5858.1mm2, adj f7,f8,f9,f10,f11
PLACE A rot(axis=(0,-1,0),1deg) t=(174.97,-124.2,-28.1)mm
PLACE B t=(-104.51,-122.33,-502.45)mm fixed
PLACE C rot(axis=(0,-1,0),133.1deg) t=(-104.51,-124.2,-389.95)mm
PLACE D rot(axis=(0,-1,0),26.9deg) t=(-286.93,-124.2,-199.87)mm
PLACE E rot(axis=(0,-1,0),1deg) t=(47.49,-124.2,-30.22)mm
MATE revolute C.f6 <-> B.f2  axis (0,1,0) through (-104.51,-141.08,-389.95)mm
MATE fastened A.f0 <-> E.f5  axis (-1,0,-0.02) through (174.97,-124.2,-28.1)mm
MATE revolute C.f20 <-> D.f11  axis (0,1,0) through (-283.96,-124.2,-198.36)mm
MATE revolute E.f0 <-> D.f6  axis (0,-1,0) through (47.49,-124.2,-30.22)mm
